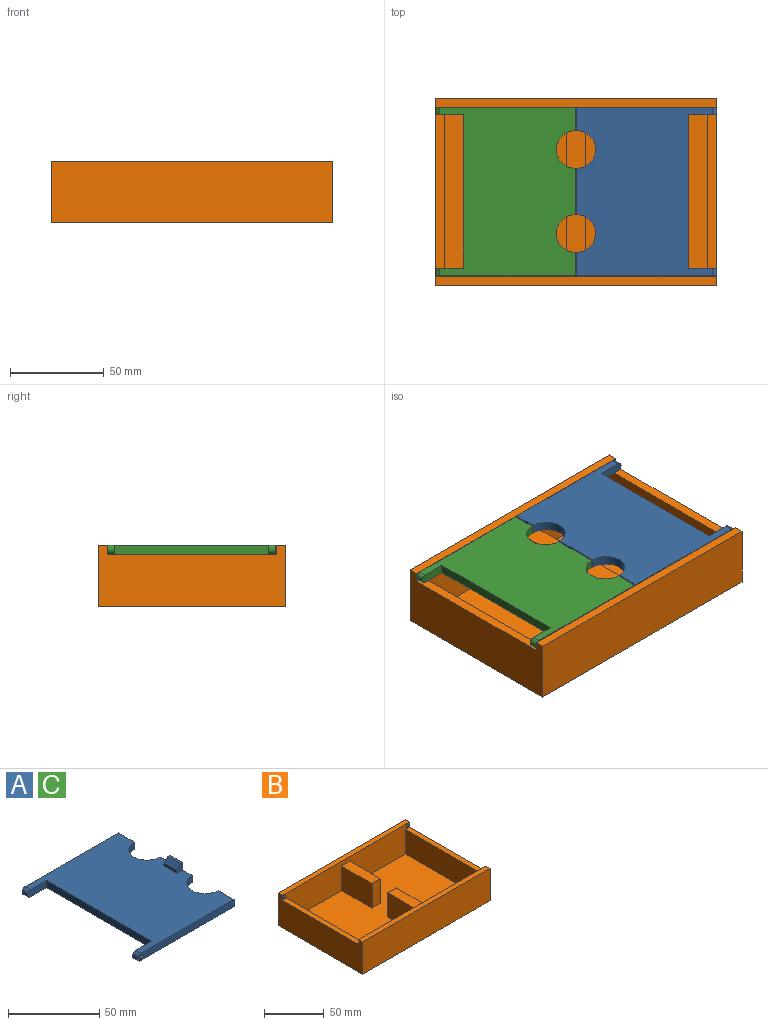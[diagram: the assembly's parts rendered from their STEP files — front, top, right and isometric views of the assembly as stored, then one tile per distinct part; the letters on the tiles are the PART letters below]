
ASSEMBLY  parts=3 mates=2
PART A: 21 faces, bbox 74.5x90.8x9.8 mm
  f0: plane 74.5x4.8mm, normal (0,1,0), area 350.2mm2, adj f3,f4,f7,f11,f20
  f1: plane 15x4.8mm, normal (0,-1,0), area 69.5mm2, adj f3,f4,f9,f20
  f2: plane 15x4.8mm, normal (0,1,0), area 69.5mm2, adj f3,f4,f9,f19
  f3: plane 89.5x72.1mm, normal (0,0,1), area 5066.9mm2, adj f0,f1,f2,f5,f6,f7,f8,f9
  f4: plane 89.5x72.1mm, normal (0,0,-1), area 5111.9mm2, adj f0,f1,f2,f5,f6,f7,f8,f9
  f5: plane 24.75x9.8mm, normal (1,0,0), area 168.8mm2, adj f3,f4,f12,f13,f14,f15,f17
  f6: plane 12.38x4.8mm, normal (1,0,0), area 59.4mm2, adj f3,f4,f8,f12
  f7: plane 12.38x4.8mm, normal (1,0,0), area 59.4mm2, adj f0,f3,f4,f13
  f8: plane 74.5x4.8mm, normal (0,-1,0), area 350.2mm2, adj f3,f4,f6,f10,f19
  f9: plane 81.5x4.8mm, normal (-1,0,0), area 391.2mm2, adj f1,f2,f3,f4
  f10: torus R=0.01mm, axis (0,0,1), area 10mm2, adj f8
  f11: torus R=0.01mm, axis (0,0,1), area 10mm2, adj f0
  f12: cylinder r=10mm len=20mm, axis (0,0,1), area 150.8mm2, adj f3,f4,f5,f6
  f13: cylinder r=10mm len=20mm, axis (0,0,1), area 150.8mm2, adj f3,f4,f5,f7
  f14: plane 5x4.5mm, normal (0,-1,0), area 18mm2, adj f3,f5,f16,f17,f18
  f15: plane 5x4.5mm, normal (0,1,0), area 18mm2, adj f3,f5,f16,f17,f18
  f16: plane 10x2mm, normal (-1,0,0), area 20mm2, adj f3,f14,f15,f18
  f17: plane 10x1.5mm, normal (0,0,1), area 15mm2, adj f5,f14,f15,f18
  f18: plane 10x3mm, normal (-0.71,0,0.71), area 42.4mm2, adj f14,f15,f16,f17
  f19: cylinder r=2.4mm len=4.8mm, axis (0,-1,0), area 30.2mm2, adj f2,f3,f4,f8
  f20: cylinder r=2.4mm len=4.8mm, axis (0,-1,0), area 30.2mm2, adj f0,f1,f3,f4
PART B: 26 faces, bbox 150x100x33 mm
  f0: plane 36.34x25mm, normal (1,0,0), area 908.5mm2, adj f13,f16,f19,f20
  f1: plane 36.34x25mm, normal (-1,0,0), area 908.5mm2, adj f13,f16,f19,f20
  f2: plane 36.34x10mm, normal (0,0,1), area 354.3mm2, adj f10,f14,f15,f21
  f3: plane 150x5mm, normal (0,0,1), area 750mm2, adj f4,f5,f6,f13
  f4: plane 100x33mm, normal (-1,0,0), area 2850mm2, adj f3,f5,f7,f8,f9,f13,f15,f17
  f5: plane 150x33mm, normal (0,-1,0), area 4950mm2, adj f3,f4,f6,f9
  f6: plane 100x33mm, normal (1,0,0), area 2850mm2, adj f3,f5,f7,f8,f9,f13,f15,f18
  f7: plane 150x33mm, normal (0,1,0), area 4950mm2, adj f4,f6,f8,f9
  f8: plane 150x5mm, normal (0,0,1), area 750mm2, adj f4,f6,f7,f15
  f9: plane 150x100mm, normal (0,0,-1), area 15000mm2, adj f4,f5,f6,f7
  f10: plane 36.34x25mm, normal (1,0,0), area 908.5mm2, adj f2,f15,f16,f21
  f11: plane 90x25mm, normal (-1,0,0), area 2250mm2, adj f13,f15,f16,f18
  f12: plane 90x25mm, normal (1,0,0), area 2250mm2, adj f13,f15,f16,f17
  f13: plane 150x30mm, normal (0,1,0), area 3985.9mm2, adj f0,f1,f3,f4,f6,f11,f12,f16
  f14: plane 36.34x25mm, normal (-1,0,0), area 908.5mm2, adj f2,f15,f16,f21
  f15: plane 150x30mm, normal (0,-1,0), area 3985.9mm2, adj f2,f4,f6,f8,f10,f11,f12,f14
  f16: plane 140x90mm, normal (0,0,1), area 11891.3mm2, adj f0,f1,f10,f11,f12,f13,f14,f15
  f17: plane 90x5mm, normal (0,0,1), area 450mm2, adj f4,f12,f13,f15
  f18: plane 90x5mm, normal (0,0,1), area 450mm2, adj f6,f11,f13,f15
  f19: plane 36.34x10mm, normal (0,0,1), area 354.3mm2, adj f0,f1,f13,f20
  f20: cylinder r=10mm len=25mm, axis (0,0,1), area 261.8mm2, adj f0,f1,f16,f19
  f21: cylinder r=10mm len=25mm, axis (0,0,1), area 261.8mm2, adj f2,f10,f14,f16
  f22: sphere r=1.5mm, area 14.1mm2, adj f15
  f23: sphere r=1.5mm, area 14.1mm2, adj f15
  f24: sphere r=1.5mm, area 14.1mm2, adj f13
  f25: sphere r=1.5mm, area 14.1mm2, adj f13
PART C: same geometry as A
PLACE A rot(axis=(0,1,0),180deg) t=(37.65,0.25,32.9)mm
PLACE B at identity fixed
PLACE C rot(axis=(-1,0,0),180deg) t=(-37.67,0.25,32.9)mm
MATE pin_slot A.f19 <-> B.f15  axis (0,1,0) through (72.5,45,30.5)mm
MATE pin_slot C.f8 <-> B.f15  axis (0,1,0) through (-72.5,45,30.5)mm
